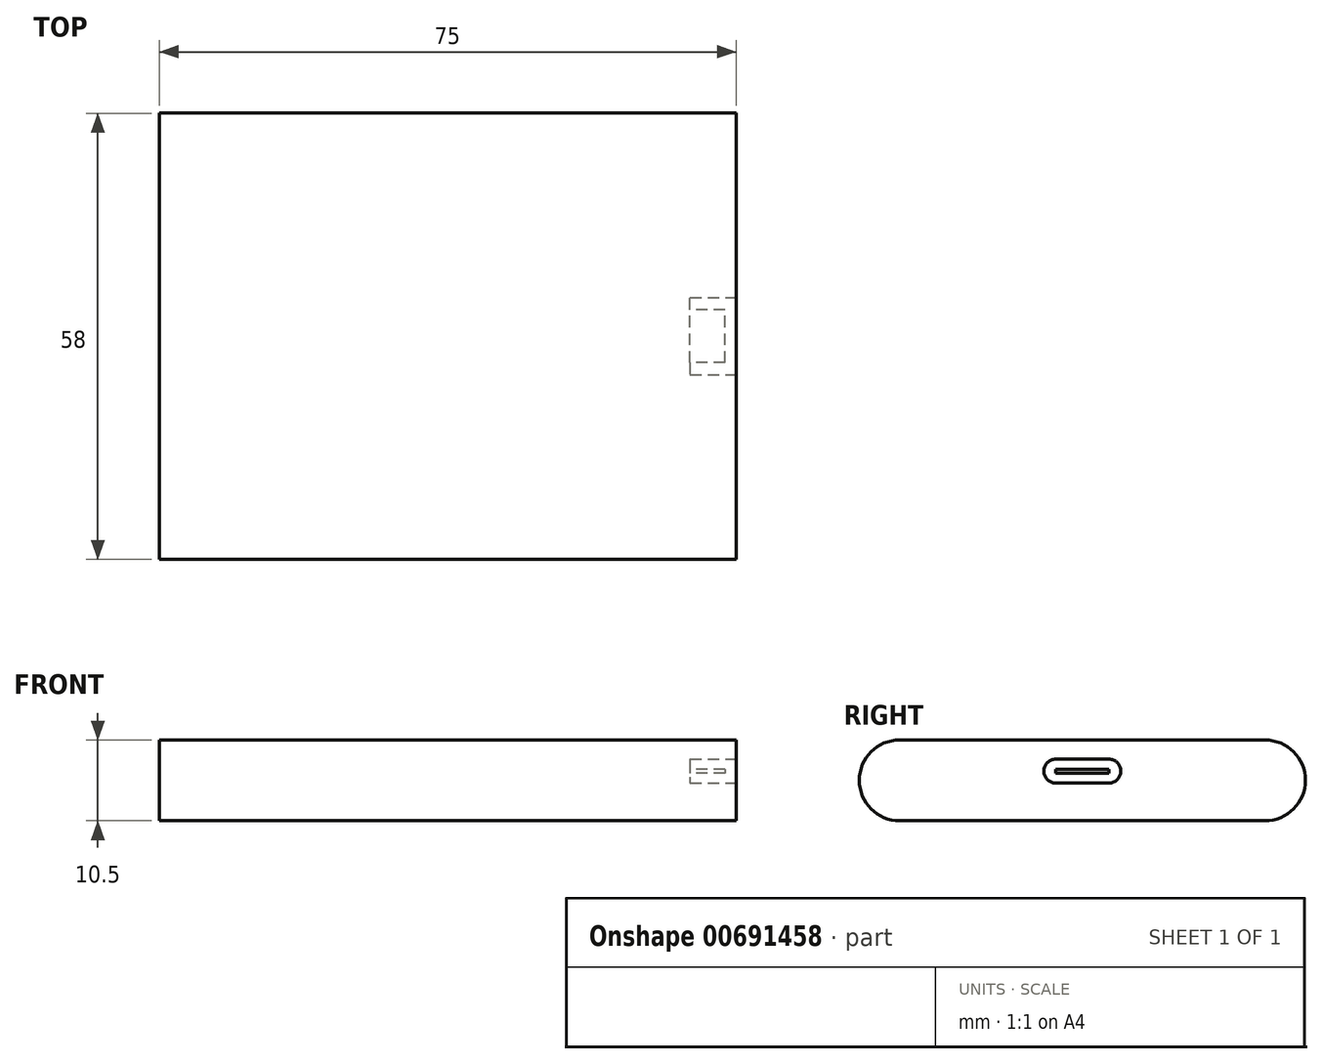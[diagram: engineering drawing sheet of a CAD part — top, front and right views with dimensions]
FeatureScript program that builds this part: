
annotation { "Feature Type Name" : "Feature", "Feature Type Description" : "" }
export const myFeature = defineFeature(function(context is Context, id is Id, definition is map)
    precondition{}
    {
        {
            var Q0;
            Q0=qCreatedBy(makeId("Top.planeOp"),FACE);
            var sketch = newSketch(context, id + "F0", { "sketchPlane" : qUnion([Q0])});
            skLineSegment(sketch, "E0.bottom", {"start": v(-55.45, -42.5) * mm, "end": v(19.55, -42.5) * mm});
            skLineSegment(sketch, "E0.top", {"start": v(-55.45, 15.5) * mm, "end": v(19.55, 15.5) * mm});
            skLineSegment(sketch, "E0.left", {"start": v(-55.45, -42.5) * mm, "end": v(-55.45, 15.5) * mm});
            skLineSegment(sketch, "E0.right", {"start": v(19.55, -42.5) * mm, "end": v(19.55, 15.5) * mm});
            skSolve(sketch);
        }
        {
            var Q0;
            Q0=makeQuery(id+"F0.imprint","IMPRINT",FACE,{"disambiguationData":[TD([[makeQuery(id+"F0.imprint","IMPRINT",EDGE,{"derivedFrom":sQuery(id+"F0.wireOp",EDGE,"E0.bottom")}),1.0]])]});
            extrude(context, id + "F1", {"entities" : qUnion([Q0]), "depth" : 10.5 * mm, "offsetDistance" : 25.4 * mm});
        }
        {
            var Q0;
            Q0=makeQuery(id+"F1.opExtrude","SWEPT_FACE",FACE,{"disambiguationData":[OSD([sQuery(id+"F0.wireOp",EDGE,"E0.right")])]});
            var sketch = newSketch(context, id + "F2", { "sketchPlane" : qUnion([Q0])});
            skLineSegment(sketch, "E1", {"start": v(-13.5, 8) * mm, "end": v(-18.5, 8) * mm});
            skLineSegment(sketch, "E2", {"start": v(-13.5, 8) * mm, "end": v(-8.5, 8) * mm});
            skLineSegment(sketch, "E3", {"start": v(-8.5, 8) * mm, "end": v(-8.5, 4.9) * mm});
            skLineSegment(sketch, "E4", {"start": v(-8.5, 4.9) * mm, "end": v(-18.5, 4.9) * mm});
            skLineSegment(sketch, "E5", {"start": v(-18.5, 4.9) * mm, "end": v(-18.5, 8) * mm});
            skCircle(sketch, "E6", {"center": v(-16.95, 6.45) * mm, "radius": 1.55 * mm});
            skCircle(sketch, "E7", {"center": v(-10.05, 6.45) * mm, "radius": 1.55 * mm});
            skLineSegment(sketch, "E8", {"start": v(-16.95, 8) * mm, "end": v(-16.95, 4.9) * mm});
            skLineSegment(sketch, "E9", {"start": v(-10.05, 8) * mm, "end": v(-10.05, 4.9) * mm});
            skSolve(sketch);
        }
        {
            var Q0;
            Q0=makeQuery(id+"F1.opExtrude","CAP_EDGE",EDGE,{"disambiguationData":[OSD([sQuery(id+"F0.wireOp",EDGE,"E0.bottom")])],"isStart":false});
            var Q1;
            Q1=makeQuery(id+"F1.opExtrude","CAP_EDGE",EDGE,{"disambiguationData":[OSD([sQuery(id+"F0.wireOp",EDGE,"E0.bottom")])],"isStart":true});
            var Q2;
            Q2=makeQuery(id+"F1.opExtrude","CAP_EDGE",EDGE,{"disambiguationData":[OSD([sQuery(id+"F0.wireOp",EDGE,"E0.top")])],"isStart":false});
            var Q3;
            Q3=makeQuery(id+"F1.opExtrude","CAP_EDGE",EDGE,{"disambiguationData":[OSD([sQuery(id+"F0.wireOp",EDGE,"E0.top")])],"isStart":true});
            fillet(context, id + "F3", {"entities" : qUnion([Q0, Q1, Q2, Q3]), "radius" : 5.25 * mm, "tangentPropagation" : true, "allowEdgeOverflow" : false});
        }
        {
            var Q0;
            {var subQ2=sQuery(id+"F2.wireOp",EDGE,"E1");var subQ6=sQuery(id+"F2.wireOp",EDGE,"E2");var subQ7=makeQuery(id+"F2.imprint","INTERSECT",VERTEX,{"derivedFrom":[subQ2,subQ6]});Q0=makeQuery(id+"F2.imprint","IMPRINT",FACE,{"disambiguationData":[TD([[makeQuery(id+"F2.imprint","IMPRINT",EDGE,{"disambiguationData":[TD([[subQ7,-1.0]])],"derivedFrom":subQ2}),1.0]])]});}
            var Q1;
            {var subQ0=sQuery(id+"F2.wireOp",EDGE,"E9");Q1=makeQuery(id+"F2.imprint","IMPRINT",FACE,{"disambiguationData":[TD([[makeQuery(id+"F2.imprint","IMPRINT",EDGE,{"derivedFrom":subQ0}),-1.0]])]});}
            var Q2;
            {var subQ0=sQuery(id+"F2.wireOp",EDGE,"E9");Q2=makeQuery(id+"F2.imprint","IMPRINT",FACE,{"disambiguationData":[TD([[makeQuery(id+"F2.imprint","IMPRINT",EDGE,{"derivedFrom":subQ0}),1.0]])]});}
            var Q3;
            {var subQ0=sQuery(id+"F2.wireOp",EDGE,"E8");Q3=makeQuery(id+"F2.imprint","IMPRINT",FACE,{"disambiguationData":[TD([[makeQuery(id+"F2.imprint","IMPRINT",EDGE,{"derivedFrom":subQ0}),1.0]])]});}
            var Q4;
            {var subQ0=sQuery(id+"F2.wireOp",EDGE,"E8");Q4=makeQuery(id+"F2.imprint","IMPRINT",FACE,{"disambiguationData":[TD([[makeQuery(id+"F2.imprint","IMPRINT",EDGE,{"derivedFrom":subQ0}),-1.0]])]});}
            extrude(context, id + "F4", {"entities" : qUnion([Q0, Q1, Q2, Q3, Q4]), "operationType" : NewBodyOperationType.REMOVE, "oppositeDirection" : true, "depth" : 6 * mm, "offsetDistance" : 25.4 * mm});
        }
        {
            var Q0;
            Q0=makeQuery(id+"F4.boolean.opBoolean","COPY",FACE,{"derivedFrom":makeQuery(id+"F4.opExtrude","CAP_FACE",FACE,{"disambiguationData":[OSD([sQuery(id+"F2.wireOp",EDGE,"E1"),sQuery(id+"F2.wireOp",EDGE,"E2"),sQuery(id+"F2.wireOp",EDGE,"E4"),sQuery(id+"F2.wireOp",EDGE,"E6"),sQuery(id+"F2.wireOp",EDGE,"E7")])],"isStart":false})});
            var sketch = newSketch(context, id + "F5", { "sketchPlane" : qUnion([Q0])});
            skLineSegment(sketch, "E10", {"start": v(-16.95, 8) * mm, "end": v(-16.95, 4.9) * mm});
            skLineSegment(sketch, "E11", {"start": v(-10.05, 8) * mm, "end": v(-10.05, 4.9) * mm});
            skLineSegment(sketch, "E12", {"start": v(-16.95, 6.45) * mm, "end": v(-10.05, 6.45) * mm});
            skLineSegment(sketch, "E13.top", {"start": v(-16.95, 6.7) * mm, "end": v(-10.05, 6.7) * mm});
            skLineSegment(sketch, "E13.left", {"start": v(-16.95, 6.45) * mm, "end": v(-16.95, 6.7) * mm});
            skLineSegment(sketch, "E13.right", {"start": v(-10.05, 6.45) * mm, "end": v(-10.05, 6.7) * mm});
            skLineSegment(sketch, "E14.left", {"start": v(-16.95, 6.45) * mm, "end": v(-16.95, 6.2) * mm});
            skLineSegment(sketch, "E14.right", {"start": v(-10.05, 6.45) * mm, "end": v(-10.05, 6.2) * mm});
            skLineSegment(sketch, "E15.top", {"start": v(-16.95, 6.2) * mm, "end": v(-10.05, 6.2) * mm});
            skSolve(sketch);
        }
        {
            var Q0;
            Q0=makeQuery(id+"F5.imprint","IMPRINT",FACE,{"disambiguationData":[TD([[makeQuery(id+"F5.imprint","IMPRINT",EDGE,{"derivedFrom":sQuery(id+"F5.wireOp",EDGE,"E13.top")}),-1.0]])]});
            var Q1;
            Q1=makeQuery(id+"F5.imprint","IMPRINT",FACE,{"disambiguationData":[TD([[makeQuery(id+"F5.imprint","IMPRINT",EDGE,{"derivedFrom":sQuery(id+"F5.wireOp",EDGE,"E12")}),-1.0]])]});
            extrude(context, id + "F6", {"entities" : qUnion([Q0, Q1]), "operationType" : NewBodyOperationType.ADD, "depth" : 4.57 * mm, "offsetDistance" : 25.4 * mm});
        }
    });
